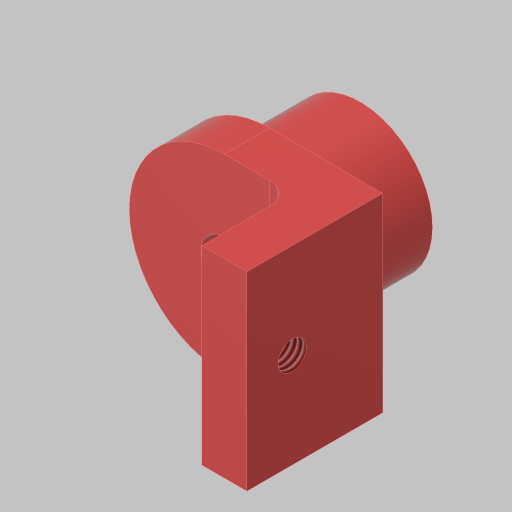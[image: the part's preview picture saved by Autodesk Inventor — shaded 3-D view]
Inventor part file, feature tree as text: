
AUTODESK INVENTOR PART (.ipt)
format: ipt  version: 2023.5 (Build 275446000, 446)  size: 148,480 bytes
history: native  units: in
note: dims shown in document units (in); Inventor stores cm internally (conversion verified against a paired STEP export)
features: sketch x5, extrude x3, hole x2, fillet x1, projected_geometry x1
ambient origin geometry x8: Origin, YZ Plane, XZ Plane, XY Plane, X Axis, Y Axis, Z Axis, Center Point
bodies: Solid1 (feature_tree)
feature tree (12):
  extrude  "Extrusion1"  Depth=0.5in TaperAngle=0.0deg
  extrude  "Extrusion2"  Depth=0.25in TaperAngle=0.0deg
  hole  "Hole2"  [1 undecoded]
  extrude  "Extrusion3"  Depth=0.25in
  fillet  "Fillet1"  Radius=0.5in
  hole  "Hole3"  [1 undecoded]
  sketch  "Sketch1"  dims[d0=0.8in d1=0.5in d2=0.0in]
  sketch  "Sketch2"  dims[d3=0.125in d4=0.25in d5=0.0in]
  sketch  "Sketch4"  dims[d6=0.688in d14=0.625in]
  sketch  "Sketch5"  dims[d15=0.257in d16=0.75in d17=0.375in d18=0.25in d19=0.5635in d20=1.0in d21=0.8108in d22=0.25in d23=0.5in d24=0.0in]
  sketch  "Sketch6"  dims[d25=0.125in d27=0.156in d28=0.38in d29=0.385in d30=0.25in d31=0.5635in d32=1.0in d33=0.8108in d35=0.25in]
  projected_geometry  "Project Cut Edges1"
note: 2 required parameter values undecoded (feature->parameter linkage not recoverable at this tier; creation-order binding heuristic only, values carry confidence <= 0.55)
